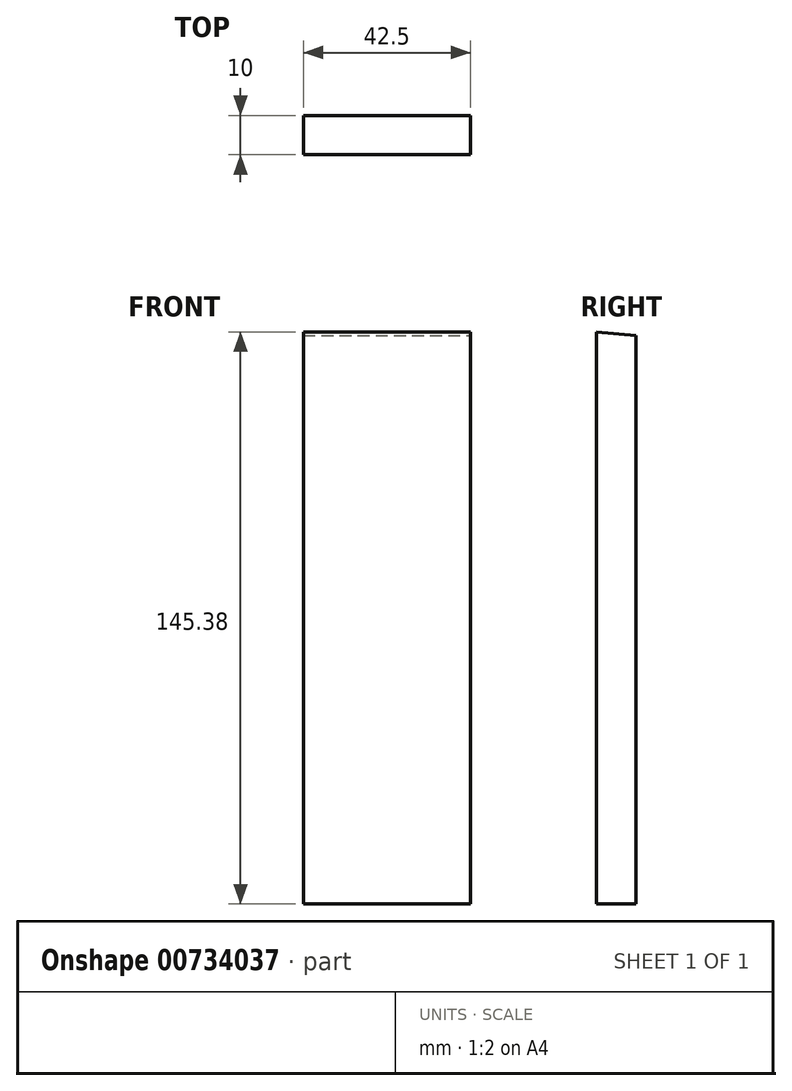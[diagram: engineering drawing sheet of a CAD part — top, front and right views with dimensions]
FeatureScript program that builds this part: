
annotation { "Feature Type Name" : "Feature", "Feature Type Description" : "" }
export const myFeature = defineFeature(function(context is Context, id is Id, definition is map)
    precondition{}
    {
        {
            var Q0;
            Q0=qCreatedBy(makeId("Front.planeOp"),FACE);
            var sketch = newSketch(context, id + "F0", { "sketchPlane" : qUnion([Q0])});
            skLineSegment(sketch, "E0.bottom", {"start": v(-47.9, 65.36) * mm, "end": v(-5.4, 65.36) * mm});
            skLineSegment(sketch, "E0.top", {"start": v(-47.9, -79.14) * mm, "end": v(-5.4, -79.14) * mm});
            skLineSegment(sketch, "E0.left", {"start": v(-47.9, 65.36) * mm, "end": v(-47.9, -79.14) * mm});
            skLineSegment(sketch, "E0.right", {"start": v(-5.4, 65.36) * mm, "end": v(-5.4, -79.14) * mm});
            skSolve(sketch);
        }
        {
            var Q0;
            Q0=qSketchRegion(id+"F0",true);
            extrude(context, id + "F1", {"entities" : qUnion([Q0]), "depth" : 10 * mm, "offsetDistance" : 25 * mm});
        }
        {
            var Q0;
            Q0=makeQuery(id+"F1.opExtrude","SWEPT_FACE",FACE,{"disambiguationData":[OSD([sQuery(id+"F0.wireOp",EDGE,"E0.right")])]});
            var sketch = newSketch(context, id + "F2", { "sketchPlane" : qUnion([Q0])});
            skLineSegment(sketch, "E1", {"start": v(-10, 65.36) * mm, "end": v(-10, 66.24) * mm});
            skLineSegment(sketch, "E2", {"start": v(-10, 66.24) * mm, "end": v(0, 65.36) * mm});
            skLineSegment(sketch, "E3", {"start": v(0, 65.36) * mm, "end": v(-10, 65.36) * mm});
            skSolve(sketch);
        }
        {
            var Q0;
            Q0=qSketchRegion(id+"F2",true);
            extrude(context, id + "F3", {"entities" : qUnion([Q0]), "operationType" : NewBodyOperationType.ADD, "oppositeDirection" : true, "depth" : 42.5 * mm, "offsetDistance" : 25 * mm});
        }
    });
